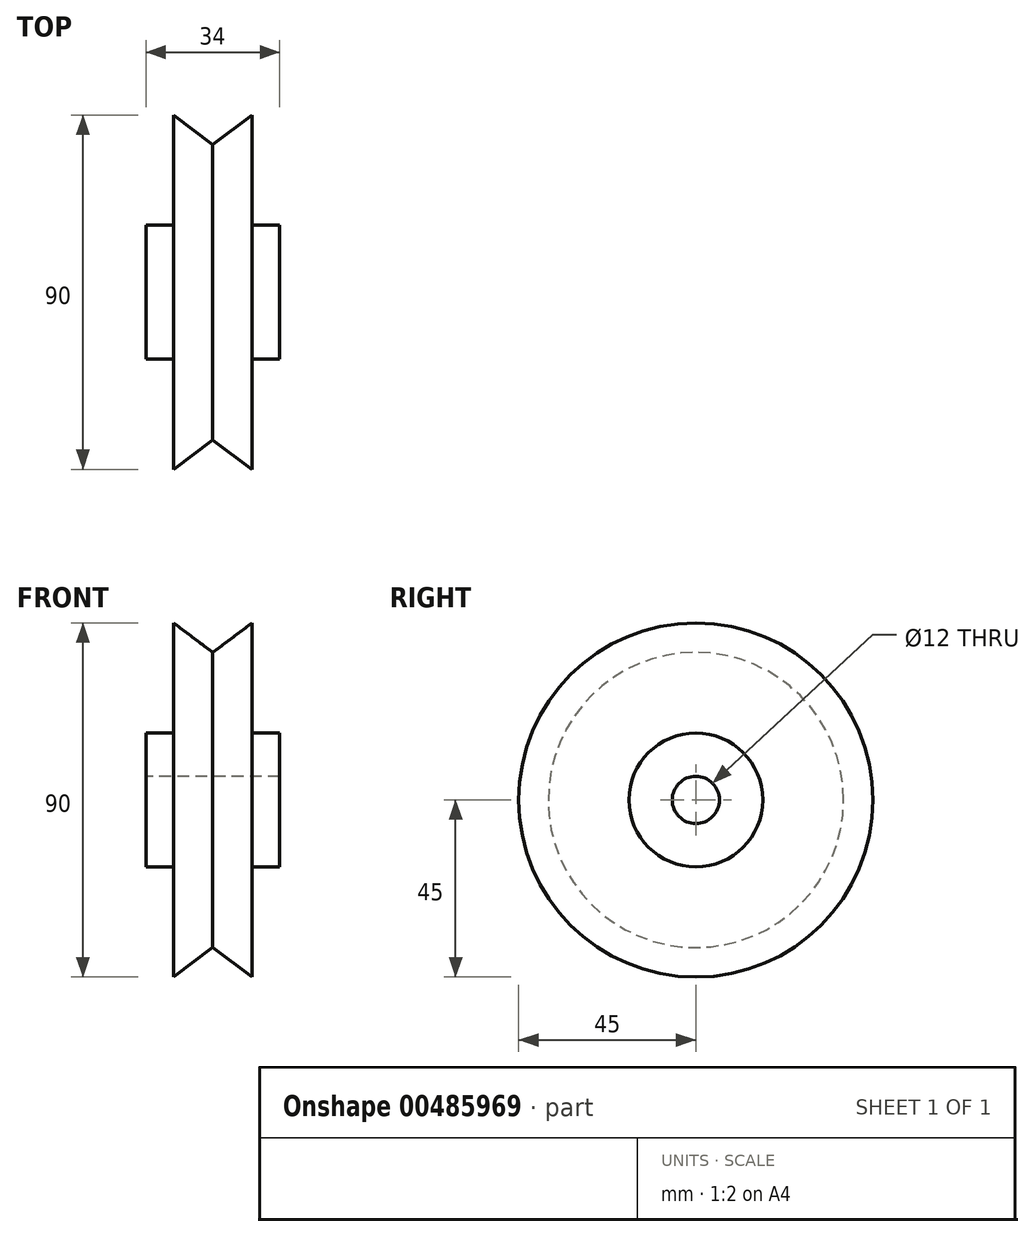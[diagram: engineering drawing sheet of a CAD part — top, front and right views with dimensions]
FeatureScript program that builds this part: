
annotation { "Feature Type Name" : "Feature", "Feature Type Description" : "" }
export const myFeature = defineFeature(function(context is Context, id is Id, definition is map)
    precondition{}
    {
        {
            var Q0;
            Q0=qCreatedBy(makeId("Top.planeOp"),FACE);
            var sketch = newSketch(context, id + "F0", { "sketchPlane" : qUnion([Q0])});
            skLineSegment(sketch, "E0", {"start": v(0, 47.97) * mm, "end": v(0, -45.27) * mm, "construction": true});
            skLineSegment(sketch, "E1", {"start": v(-40.81, 0) * mm, "end": v(48.24, 0) * mm, "construction": true});
            skLineSegment(sketch, "E2", {"start": v(-17, 6) * mm, "end": v(0, 6) * mm});
            skLineSegment(sketch, "E3", {"start": v(-17, 6) * mm, "end": v(-17, 17) * mm});
            skLineSegment(sketch, "E4", {"start": v(-17, 17) * mm, "end": v(-10, 17) * mm});
            skLineSegment(sketch, "E5", {"start": v(-10, 17) * mm, "end": v(-10, 45) * mm});
            skLineSegment(sketch, "E6", {"start": v(-10, 45) * mm, "end": v(0, 37.5) * mm});
            skLineSegment(sketch, "E7.MirrorCS", {"start": v(10, 45) * mm, "end": v(0, 37.5) * mm});
            skLineSegment(sketch, "E8.MirrorCS", {"start": v(10, 17) * mm, "end": v(10, 45) * mm});
            skLineSegment(sketch, "E9.MirrorCS", {"start": v(17, 6) * mm, "end": v(0, 6) * mm});
            skLineSegment(sketch, "E10.MirrorCS", {"start": v(17, 6) * mm, "end": v(17, 17) * mm});
            skLineSegment(sketch, "E11.MirrorCS", {"start": v(17, 17) * mm, "end": v(10, 17) * mm});
            skSolve(sketch);
        }
        {
            var Q0;
            Q0=makeQuery(id+"F0.imprint","IMPRINT",FACE,{"disambiguationData":[TD([[makeQuery(id+"F0.imprint","IMPRINT",EDGE,{"derivedFrom":sQuery(id+"F0.wireOp",EDGE,"E2")}),1.0]])]});
            var Q1;
            Q1=sQuery(id+"F0.wireOp",EDGE,"E1");
            revolve(context, id + "F1", {"entities" : qUnion([Q0]), "axis" : qUnion([Q1]), "revolveType" : RevolveType.FULL});
        }
    });
